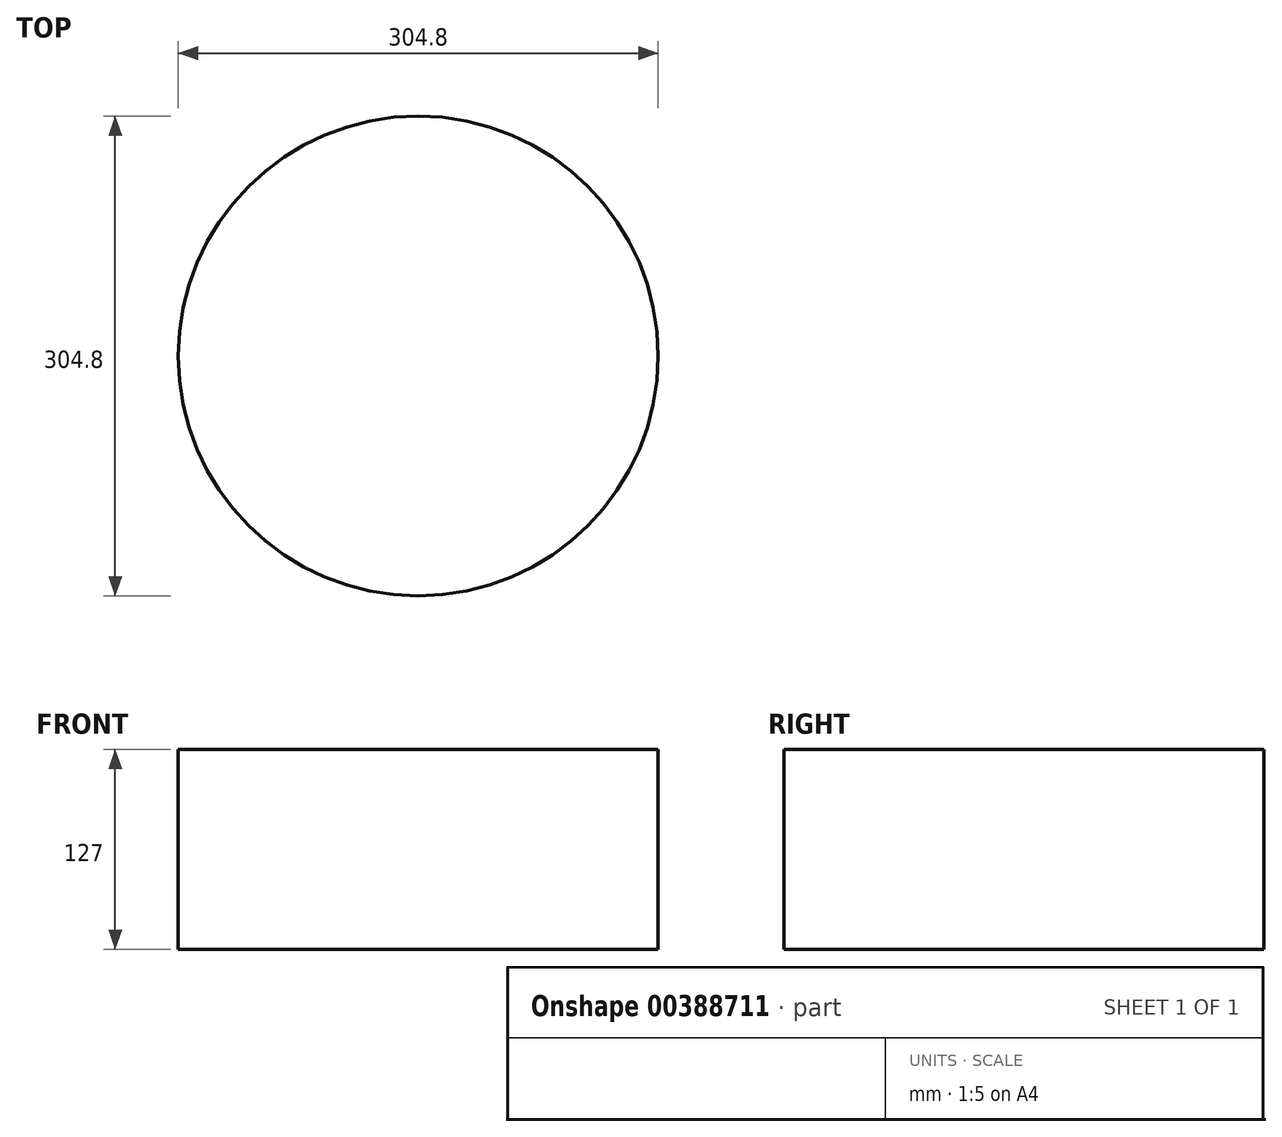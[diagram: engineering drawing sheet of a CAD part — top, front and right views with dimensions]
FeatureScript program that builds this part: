
annotation { "Feature Type Name" : "Feature", "Feature Type Description" : "" }
export const myFeature = defineFeature(function(context is Context, id is Id, definition is map)
    precondition{}
    {
        {
            var Q0;
            Q0=qCreatedBy(makeId("Top.planeOp"),FACE);
            var sketch = newSketch(context, id + "F0", { "sketchPlane" : qUnion([Q0])});
            skLineSegment(sketch, "E0", {"start": v(-633.56, -916.34) * mm, "end": v(-633.56, 1115.66) * mm});
            skCircle(sketch, "E1", {"center": v(-633.56, 1115.66) * mm, "radius": 152.4 * mm});
            skSolve(sketch);
        }
        {
            var Q0;
            Q0=makeQuery(id+"F0.imprint","IMPRINT",FACE,{"disambiguationData":[TD([[makeQuery(id+"F0.imprint","IMPRINT",EDGE,{"derivedFrom":sQuery(id+"F0.wireOp",EDGE,"E1")}),1.0]])]});
            extrude(context, id + "F1", {"entities" : qUnion([Q0]), "depth" : 127 * mm});
        }
    });
